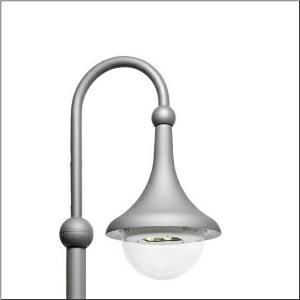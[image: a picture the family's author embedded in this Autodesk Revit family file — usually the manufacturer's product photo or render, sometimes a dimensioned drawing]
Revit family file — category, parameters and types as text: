
# Revit family: kleine_glocke_iq___st1_2a_5xa1575e1v108_a1ae
name_source: partatom
category: Lighting Fixtures
units: mm (PartAtom-declared; Revit-internal decimal feet)

## family parameters
Cut with Voids When Loaded = No
Host = Face
Light Source = No
Part Type = Normal
Room Calculation Point = No
Round Connector Dimension = Use Diameter
Shared = No

## types (1)
- --- (1 x LED, 3220 lm, 20.1 W, 3000K)
    Apparent Load = 20 VA
    CIE Flux Codes = 28 65 95 100 100
    Color Rendering = 70
    Color Temperature = 3000K
    Default Elevation = 1800 mm
    Description = Small Bell iQ, mast luminaire, primary light control with 3 zone facetted reflector, of plastic, silver coated, primary optical cover: enclosure, of PMMA, transparent, light distribution: ST1.2a, light emission: direct distribution, primary light characteristic: asymmetric, installation type: suspended mounting, High Power LED, rated luminous flux: 3.220lm, luminous efficacy: 160lm/W, light colour: 730, colour temperature: 3000K, control gear: iQ-Street Remote, D4i with power reduction, control: optimised constant luminous flux control (CLO 2.0), Desk-Remote (wireless, voltage-free reading and setting of iQ features in the workshop via application-optimized NFC function/RFID function), Light-Fading, Smart-Wire, Night-Set, Lumen-Switch, Temp-Guard, Auto-Match, Street-Remote, pre-setting: logarithmic dimming characteristic, mains connection: 230..240V, AC, 50/60Hz, start of lifetime: 20W, end of service life: 21W, reduction: 10W, luminaire housing, bell-shaped, of glass-fibre reinforced polyester, coated, Siteco® metallic grey (DB 702S), please order curved mast extension separately, diameter: 430mm, height: 575mm, mounting height: 2.5..4.0m, Smart Interface above, protection rating (complete): IP54, insulation class (complete): insulation class II (safety insulation), certification: CE, ENEC, VDE, impact resistance: IK09, standard-compliant lighting for roads and squares, packaging unit: 1 piece

Light Distribution: ST1.2a
    Height = 575 mm
    Lamp = 1 x LED
    Lamp Light Flux = 3220 lm
    Lamp Power = 20.1 W
    Lamp count = 1
    Length = 430 mm
    Luminous efficacy = 160 lm/W
    Manufacturer = Siteco
    ModVariant = No
    Model = 5XA1575E1V108
    Number of Poles = 1
    OnlyDefault = Yes
    Power Factor = 1
    Product Name = Kleine Glocke iQ | ST1.2a
    Product group = mast luminaire | pylon annexe
    ProductGroupID = 6200
    Protection Class = Protection class II
    Protection Degree = IP 54
    RLX_Detail_Level = 1
    RLX_Emergency_Light_Flux = 0 lm
    RLX_Emergency_Type = 0
    RLX_Emergency_Type_DB = No
    RlxData = <blob elided: 73749 chars, md5=92a89fa0>
    Socket = socket
    Standby Power = 0 W
    System Light Flux = 3220 lm
    System Power = 20 W
    Type Comments = factory setting: luminous flux: 100 % | dim-lin: 254 | 376 mA
    Type Image = l_1347699.jpg
    URL = http://relux.com
    VarID = @adj_066389
    Voltage = 0 V
    Weight = 0.00 kg
    Width = 0 mm  [stored 0 ft]

note: [stored X ft] marks values corroborated as IEEE doubles in the binary element streams (Revit-internal decimal feet)

## geometry (parser evidence)
native form markers: Blend x4, Sweep x11
no freeform markers — native parametric forms only
